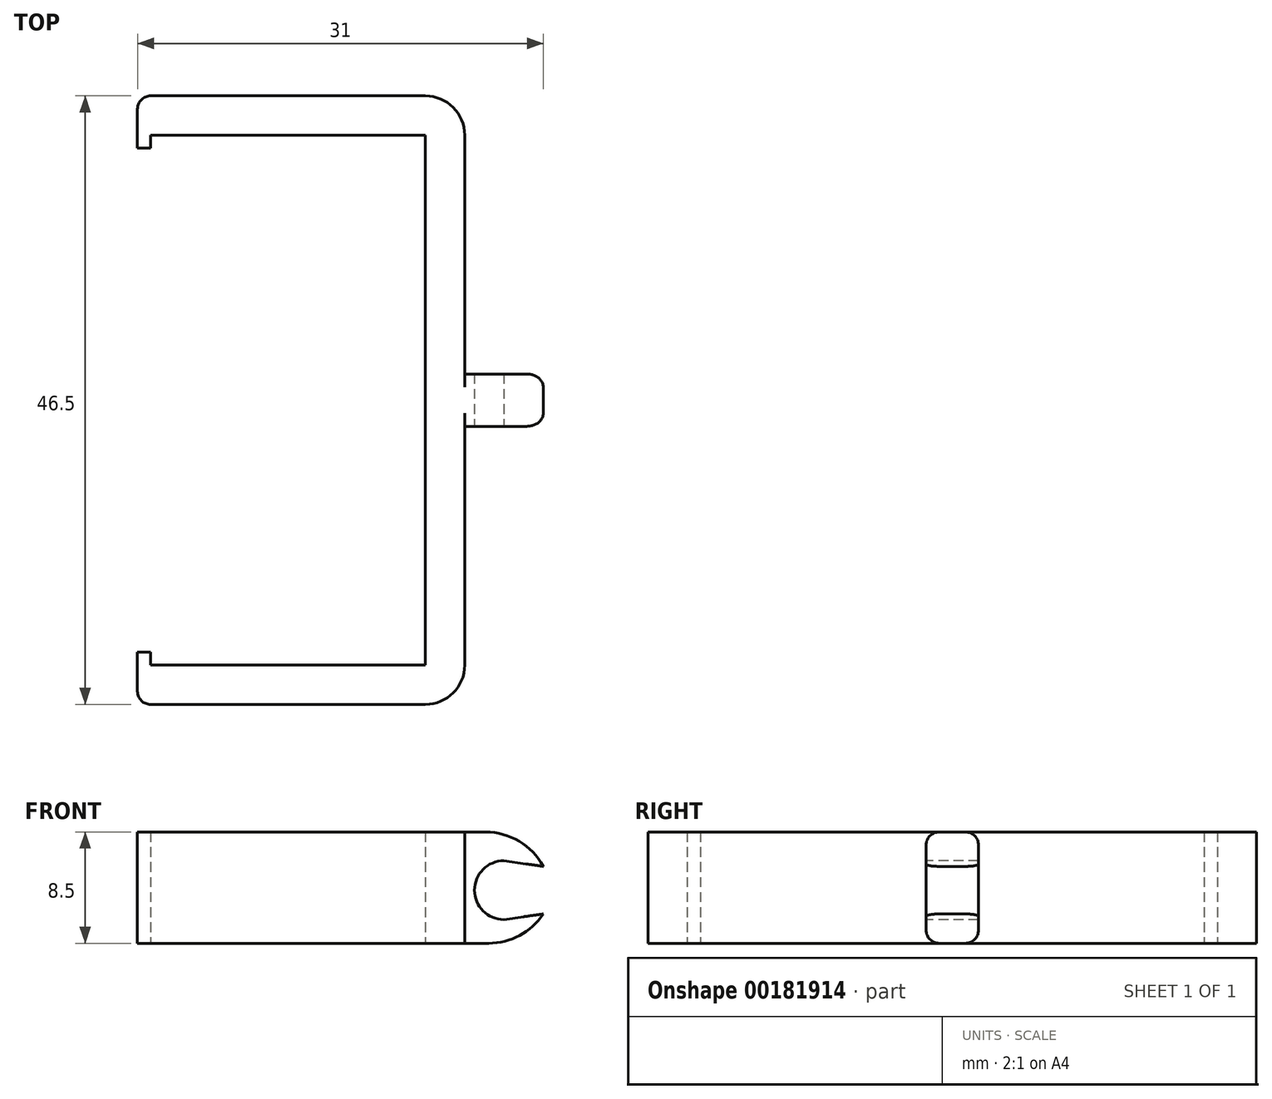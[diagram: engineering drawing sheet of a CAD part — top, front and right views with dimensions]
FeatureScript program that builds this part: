
annotation { "Feature Type Name" : "Feature", "Feature Type Description" : "" }
export const myFeature = defineFeature(function(context is Context, id is Id, definition is map)
    precondition{}
    {
        {
            var Q0;
            Q0=qCreatedBy(makeId("Top.planeOp"),FACE);
            var sketch = newSketch(context, id + "F0", { "sketchPlane" : qUnion([Q0])});
            skLineSegment(sketch, "E0", {"start": v(16.58, 28.27) * mm, "end": v(16.58, -12.23) * mm});
            skLineSegment(sketch, "E1", {"start": v(16.58, 28.27) * mm, "end": v(-4.42, 28.27) * mm});
            skLineSegment(sketch, "E2", {"start": v(16.58, -12.23) * mm, "end": v(-4.42, -12.23) * mm});
            skLineSegment(sketch, "E3", {"start": v(-4.42, -12.23) * mm, "end": v(-4.42, -11.23) * mm});
            skLineSegment(sketch, "E4", {"start": v(-4.42, 28.27) * mm, "end": v(-4.42, 27.27) * mm});
            skLineSegment(sketch, "E5.0", {"start": v(-5.42, 27.27) * mm, "end": v(-5.42, 27.27) * mm});
            skLineSegment(sketch, "E6.0", {"start": v(-5.42, -13.23) * mm, "end": v(-5.42, -11.23) * mm});
            skLineSegment(sketch, "E7.0", {"start": v(16.58, -15.23) * mm, "end": v(-4.42, -15.23) * mm});
            skLineSegment(sketch, "E8.0", {"start": v(16.58, 31.27) * mm, "end": v(-4.42, 31.27) * mm});
            skLineSegment(sketch, "E9.0", {"start": v(19.58, 27.27) * mm, "end": v(19.58, -13.23) * mm});
            skLineSegment(sketch, "E10", {"start": v(-5.42, 27.27) * mm, "end": v(-5.42, 31.27) * mm});
            skLineSegment(sketch, "E11", {"start": v(-4.42, 31.27) * mm, "end": v(-5.42, 31.27) * mm});
            skLineSegment(sketch, "E12", {"start": v(16.58, 31.27) * mm, "end": v(19.58, 31.27) * mm});
            skLineSegment(sketch, "E13", {"start": v(19.58, 27.27) * mm, "end": v(19.58, 31.27) * mm});
            skLineSegment(sketch, "E14", {"start": v(-4.42, 27.27) * mm, "end": v(-5.42, 27.27) * mm});
            skLineSegment(sketch, "E15", {"start": v(19.58, -13.23) * mm, "end": v(19.58, -15.23) * mm});
            skLineSegment(sketch, "E16", {"start": v(16.58, -15.23) * mm, "end": v(19.58, -15.23) * mm});
            skLineSegment(sketch, "E17", {"start": v(-5.42, -13.23) * mm, "end": v(-5.42, -15.23) * mm});
            skLineSegment(sketch, "E18", {"start": v(-4.42, -15.23) * mm, "end": v(-5.42, -15.23) * mm});
            skLineSegment(sketch, "E19", {"start": v(-4.42, -11.23) * mm, "end": v(-5.42, -11.23) * mm});
            skSolve(sketch);
        }
        {
            var Q0;
            Q0=makeQuery(id+"F0.imprint","IMPRINT",FACE,{"disambiguationData":[TD([[makeQuery(id+"F0.imprint","IMPRINT",EDGE,{"derivedFrom":sQuery(id+"F0.wireOp",EDGE,"E0")}),1.0]])]});
            extrude(context, id + "F1", {"entities" : qUnion([Q0]), "depth" : 8.5 * mm});
        }
        {
            var Q0;
            Q0=makeQuery(id+"F1.opExtrude","SWEPT_FACE",FACE,{"disambiguationData":[OSD([sQuery(id+"F0.wireOp",EDGE,"E9.0"),sQuery(id+"F0.wireOp",EDGE,"E13"),sQuery(id+"F0.wireOp",EDGE,"E15")])]});
            var sketch = newSketch(context, id + "F2", { "sketchPlane" : qUnion([Q0])});
            skPoint(sketch, "E20.endSnap0", {"position": v(8.02, 8.5) * mm});
            skLineSegment(sketch, "E21", {"start": v(8.02, 8.5) * mm, "end": v(8.02, 0) * mm, "construction": true});
            skLineSegment(sketch, "E22", {"start": v(-15.23, 4.25) * mm, "end": v(31.27, 4.25) * mm, "construction": true});
            skLineSegment(sketch, "E23.bottom", {"start": v(10.02, 8.5) * mm, "end": v(6.02, 8.5) * mm});
            skLineSegment(sketch, "E23.top", {"start": v(10.02, 0) * mm, "end": v(6.02, 0) * mm});
            skLineSegment(sketch, "E23.left", {"start": v(10.02, 8.5) * mm, "end": v(10.02, 0) * mm});
            skLineSegment(sketch, "E23.right", {"start": v(6.02, 8.5) * mm, "end": v(6.02, 0) * mm});
            skPoint(sketch, "E23.middle", {"position": v(8.02, 4.25) * mm});
            skSolve(sketch);
        }
        {
            var Q0;
            Q0=qSketchRegion(id+"F2",true);
            extrude(context, id + "F3", {"entities" : qUnion([Q0]), "operationType" : NewBodyOperationType.ADD, "depth" : 6 * mm});
        }
        {
            var Q0;
            Q0=makeQuery(id+"F3.opExtrude","SWEPT_FACE",FACE,{"disambiguationData":[OSD([sQuery(id+"F2.wireOp",EDGE,"E23.right")])]});
            var sketch = newSketch(context, id + "F4", { "sketchPlane" : qUnion([Q0])});
            skArc(sketch, "E24", {"start": v(22.57, 6.3) * mm, "mid": v(20.32, 4.06) * mm, "end": v(22.57, 1.8) * mm});
            skLineSegment(sketch, "E25", {"start": v(25.57, 5.87) * mm, "end": v(22.57, 6.3) * mm});
            skLineSegment(sketch, "E26", {"start": v(25.57, 5.87) * mm, "end": v(25.57, 2.24) * mm});
            skLineSegment(sketch, "E27", {"start": v(22.57, 1.8) * mm, "end": v(25.57, 2.24) * mm});
            skLineSegment(sketch, "E28", {"start": v(22.57, 4.06) * mm, "end": v(25.58, 4.06) * mm, "construction": true});
            skLineSegment(sketch, "E29", {"start": v(22.57, 4.06) * mm, "end": v(22.57, 8.5) * mm, "construction": true});
            skSolve(sketch);
        }
        {
            var Q0;
            Q0=makeQuery(id+"F4.imprint","IMPRINT",FACE,{"disambiguationData":[TD([[makeQuery(id+"F4.imprint","IMPRINT",EDGE,{"derivedFrom":sQuery(id+"F4.wireOp",EDGE,"E24")}),1.0]])]});
            var Q1;
            Q1=sQuery(id+"F4.wireOp",EDGE,"E25");
            var Q2;
            Q2=sQuery(id+"F4.wireOp",EDGE,"E24");
            var Q3;
            Q3=sQuery(id+"F4.wireOp",EDGE,"C4R9Oy1y-7e1z-FXny-91y1-kyaZ4qe8YO9C");
            var Q4;
            Q4=sQuery(id+"F4.wireOp",EDGE,"JZYNILZq-mjDS-Zgyg-Tk2O-Pl40O7umI2Ae");
            extrude(context, id + "F5", {"entities" : qUnion([Q0]), "operationType" : NewBodyOperationType.REMOVE, "surfaceEntities" : qUnion([Q1, Q2, Q3, Q4]), "oppositeDirection" : true, "depth" : 25 * mm});
        }
        {
            var Q0;
            Q0=makeQuery(id+"F3.opExtrude","CAP_EDGE",EDGE,{"disambiguationData":[OSD([sQuery(id+"F2.wireOp",EDGE,"E23.bottom")])],"isStart":false});
            var Q1;
            Q1=makeQuery(id+"F3.opExtrude","CAP_EDGE",EDGE,{"disambiguationData":[OSD([sQuery(id+"F2.wireOp",EDGE,"E23.top")])],"isStart":false});
            fillet(context, id + "F6", {"entities" : qUnion([Q0, Q1]), "radius" : 5 * mm, "tangentPropagation" : true, "allowEdgeOverflow" : false});
        }
        {
            var Q0;
            Q0=makeQuery(id+"F1.opExtrude","SWEPT_EDGE",EDGE,{"disambiguationData":[OSD([sQuery(id+"F0.wireOp",EDGE,"E15"),sQuery(id+"F0.wireOp",EDGE,"E16")])]});
            var Q1;
            Q1=makeQuery(id+"F1.opExtrude","SWEPT_EDGE",EDGE,{"disambiguationData":[OSD([sQuery(id+"F0.wireOp",EDGE,"E12"),sQuery(id+"F0.wireOp",EDGE,"E13")])]});
            fillet(context, id + "F7", {"entities" : qUnion([Q0, Q1]), "radius" : 3 * mm, "tangentPropagation" : true, "allowEdgeOverflow" : false});
        }
        {
            var Q0;
            Q0=makeQuery(id+"F1.opExtrude","SWEPT_EDGE",EDGE,{"disambiguationData":[OSD([sQuery(id+"F0.wireOp",EDGE,"E17"),sQuery(id+"F0.wireOp",EDGE,"E18")])]});
            var Q1;
            Q1=makeQuery(id+"F1.opExtrude","SWEPT_EDGE",EDGE,{"disambiguationData":[OSD([sQuery(id+"F0.wireOp",EDGE,"E10"),sQuery(id+"F0.wireOp",EDGE,"E11")])]});
            var Q2;
            Q2=makeQuery(id+"F6.opFillet","BLEND_EDGE",EDGE,{"blendedFrom":[makeQuery(id+"F3.opExtrude","CAP_EDGE",EDGE,{"disambiguationData":[OSD([sQuery(id+"F2.wireOp",EDGE,"ZQLkjopL-ZP7a-4cv0-UlQd-ru3bmJu4S5Vw.left")])],"isStart":false}),makeQuery(id+"F3.opExtrude","SWEPT_FACE",FACE,{"disambiguationData":[OSD([sQuery(id+"F2.wireOp",EDGE,"ZQLkjopL-ZP7a-4cv0-UlQd-ru3bmJu4S5Vw.bottom")])]})],"blendedInto":[makeQuery(id+"F3.opExtrude","SWEPT_FACE",FACE,{"disambiguationData":[OSD([sQuery(id+"F2.wireOp",EDGE,"ZQLkjopL-ZP7a-4cv0-UlQd-ru3bmJu4S5Vw.bottom")])]})]});
            var Q3;
            Q3=makeQuery(id+"F6.opFillet","BLEND_EDGE",EDGE,{"blendedFrom":[makeQuery(id+"F3.opExtrude","CAP_EDGE",EDGE,{"disambiguationData":[OSD([sQuery(id+"F2.wireOp",EDGE,"ZQLkjopL-ZP7a-4cv0-UlQd-ru3bmJu4S5Vw.left")])],"isStart":false}),makeQuery(id+"F3.opExtrude","SWEPT_FACE",FACE,{"disambiguationData":[OSD([sQuery(id+"F2.wireOp",EDGE,"ZQLkjopL-ZP7a-4cv0-UlQd-ru3bmJu4S5Vw.top")])]})],"blendedInto":[makeQuery(id+"F3.opExtrude","SWEPT_FACE",FACE,{"disambiguationData":[OSD([sQuery(id+"F2.wireOp",EDGE,"ZQLkjopL-ZP7a-4cv0-UlQd-ru3bmJu4S5Vw.top")])]})]});
            var Q4;
            Q4=makeQuery(id+"F6.opFillet","BLEND_EDGE",EDGE,{"blendedFrom":[makeQuery(id+"F3.opExtrude","CAP_EDGE",EDGE,{"disambiguationData":[OSD([sQuery(id+"F2.wireOp",EDGE,"ZQLkjopL-ZP7a-4cv0-UlQd-ru3bmJu4S5Vw.right")])],"isStart":false}),makeQuery(id+"F3.opExtrude","SWEPT_FACE",FACE,{"disambiguationData":[OSD([sQuery(id+"F2.wireOp",EDGE,"ZQLkjopL-ZP7a-4cv0-UlQd-ru3bmJu4S5Vw.top")])]})],"blendedInto":[makeQuery(id+"F3.opExtrude","SWEPT_FACE",FACE,{"disambiguationData":[OSD([sQuery(id+"F2.wireOp",EDGE,"ZQLkjopL-ZP7a-4cv0-UlQd-ru3bmJu4S5Vw.top")])]})]});
            var Q5;
            Q5=makeQuery(id+"F6.opFillet","BLEND_EDGE",EDGE,{"blendedFrom":[makeQuery(id+"F3.opExtrude","CAP_EDGE",EDGE,{"disambiguationData":[OSD([sQuery(id+"F2.wireOp",EDGE,"ZQLkjopL-ZP7a-4cv0-UlQd-ru3bmJu4S5Vw.right")])],"isStart":false}),makeQuery(id+"F3.opExtrude","SWEPT_FACE",FACE,{"disambiguationData":[OSD([sQuery(id+"F2.wireOp",EDGE,"ZQLkjopL-ZP7a-4cv0-UlQd-ru3bmJu4S5Vw.bottom")])]})],"blendedInto":[makeQuery(id+"F3.opExtrude","SWEPT_FACE",FACE,{"disambiguationData":[OSD([sQuery(id+"F2.wireOp",EDGE,"ZQLkjopL-ZP7a-4cv0-UlQd-ru3bmJu4S5Vw.bottom")])]})]});
            var Q6;
            Q6=makeQuery(id+"F6.opFillet","BLEND_EDGE",EDGE,{"blendedFrom":[makeQuery(id+"F3.opExtrude","CAP_EDGE",EDGE,{"disambiguationData":[OSD([sQuery(id+"F2.wireOp",EDGE,"E23.bottom")])],"isStart":false}),makeQuery(id+"F3.opExtrude","SWEPT_FACE",FACE,{"disambiguationData":[OSD([sQuery(id+"F2.wireOp",EDGE,"E23.left")])]})],"blendedInto":[makeQuery(id+"F3.opExtrude","SWEPT_FACE",FACE,{"disambiguationData":[OSD([sQuery(id+"F2.wireOp",EDGE,"E23.left")])]})]});
            var Q7;
            Q7=makeQuery(id+"F6.opFillet","BLEND_EDGE",EDGE,{"blendedFrom":[makeQuery(id+"F3.opExtrude","CAP_EDGE",EDGE,{"disambiguationData":[OSD([sQuery(id+"F2.wireOp",EDGE,"E23.top")])],"isStart":false}),makeQuery(id+"F3.opExtrude","SWEPT_FACE",FACE,{"disambiguationData":[OSD([sQuery(id+"F2.wireOp",EDGE,"E23.left")])]})],"blendedInto":[makeQuery(id+"F3.opExtrude","SWEPT_FACE",FACE,{"disambiguationData":[OSD([sQuery(id+"F2.wireOp",EDGE,"E23.left")])]})]});
            var Q8;
            Q8=makeQuery(id+"F6.opFillet","BLEND_EDGE",EDGE,{"blendedFrom":[makeQuery(id+"F3.opExtrude","CAP_EDGE",EDGE,{"disambiguationData":[OSD([sQuery(id+"F2.wireOp",EDGE,"E23.bottom")])],"isStart":false}),makeQuery(id+"F3.opExtrude","SWEPT_FACE",FACE,{"disambiguationData":[OSD([sQuery(id+"F2.wireOp",EDGE,"E23.right")])]})],"blendedInto":[makeQuery(id+"F3.opExtrude","SWEPT_FACE",FACE,{"disambiguationData":[OSD([sQuery(id+"F2.wireOp",EDGE,"E23.right")])]})]});
            var Q9;
            Q9=makeQuery(id+"F6.opFillet","BLEND_EDGE",EDGE,{"blendedFrom":[makeQuery(id+"F3.opExtrude","CAP_EDGE",EDGE,{"disambiguationData":[OSD([sQuery(id+"F2.wireOp",EDGE,"E23.top")])],"isStart":false}),makeQuery(id+"F3.opExtrude","SWEPT_FACE",FACE,{"disambiguationData":[OSD([sQuery(id+"F2.wireOp",EDGE,"E23.right")])]})],"blendedInto":[makeQuery(id+"F3.opExtrude","SWEPT_FACE",FACE,{"disambiguationData":[OSD([sQuery(id+"F2.wireOp",EDGE,"E23.right")])]})]});
            fillet(context, id + "F8", {"entities" : qUnion([Q0, Q1, Q2, Q3, Q4, Q5, Q6, Q7, Q8, Q9]), "radius" : 1 * mm, "tangentPropagation" : true, "allowEdgeOverflow" : false});
        }
    });
